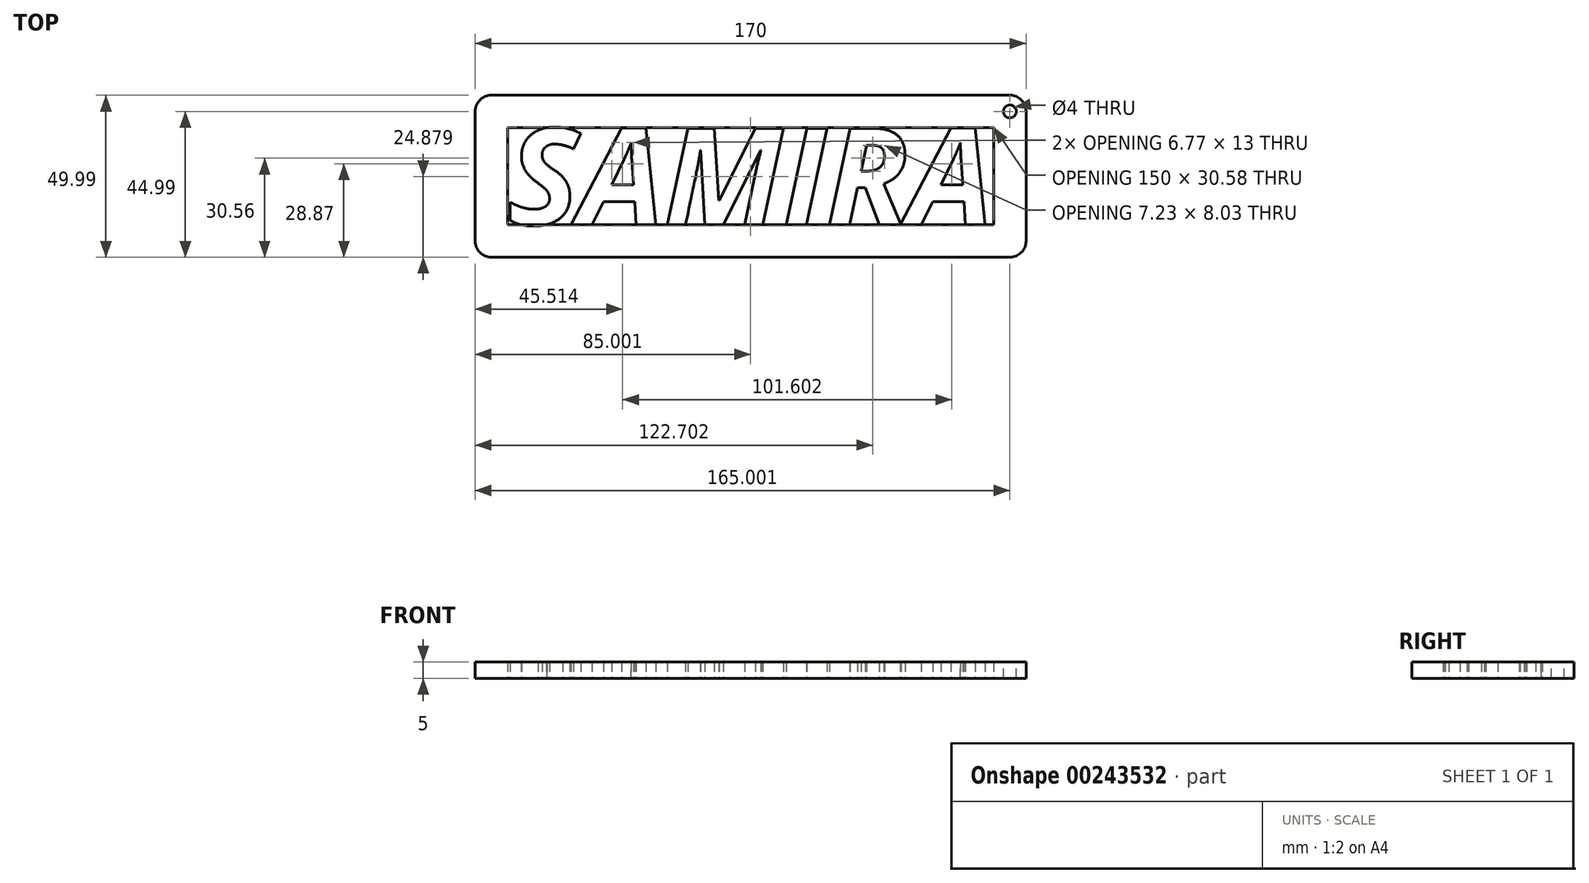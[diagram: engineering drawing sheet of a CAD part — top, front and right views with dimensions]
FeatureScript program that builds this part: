
annotation { "Feature Type Name" : "Feature", "Feature Type Description" : "" }
export const myFeature = defineFeature(function(context is Context, id is Id, definition is map)
    precondition{}
    {
        {
            var Q0;
            Q0=qCreatedBy(makeId("Top.planeOp"),FACE);
            var sketch = newSketch(context, id + "F0", { "sketchPlane" : qUnion([Q0])});
            skText(sketch, "E0", { "text": "SAMIRA", "fontName": "OpenSans-BoldItalic.ttf"});
            skLineSegment(sketch, "E1.bottom", {"start": v(-105.66, 38.68) * mm, "end": v(44.34, 38.68) * mm});
            skLineSegment(sketch, "E1.top", {"start": v(-105.66, 8.69) * mm, "end": v(44.34, 8.69) * mm});
            skLineSegment(sketch, "E1.left", {"start": v(-105.66, 38.68) * mm, "end": v(-105.66, 8.69) * mm});
            skLineSegment(sketch, "E1.right", {"start": v(44.34, 38.68) * mm, "end": v(44.34, 8.69) * mm});
            skLineSegment(sketch, "E2.bottom", {"start": v(-115.66, 48.68) * mm, "end": v(54.34, 48.68) * mm});
            skLineSegment(sketch, "E2.top", {"start": v(-115.66, -1.31) * mm, "end": v(54.34, -1.31) * mm});
            skLineSegment(sketch, "E2.left", {"start": v(-115.66, 48.68) * mm, "end": v(-115.66, -1.31) * mm});
            skLineSegment(sketch, "E2.right", {"start": v(54.34, 48.68) * mm, "end": v(54.34, -1.31) * mm});
            const initialGuessF0  = {"E0": [-0.10566, 0.00869, 1, 0, 0.03]};
            skSetInitialGuess(sketch, initialGuessF0);
            skSolve(sketch);
        }
        {
            var Q0;
            {var subQ9=sQuery(id+"F0.wireOp",EDGE,"E0.sketch_text.stroke-0");Q0=makeQuery(id+"F0.imprint","IMPRINT",FACE,{"disambiguationData":[TD([[makeQuery(id+"F0.imprint","IMPRINT",EDGE,{"derivedFrom":subQ9}),-1.0]])]});}
            var Q1;
            Q1=makeQuery(id+"F0.imprint","IMPRINT",FACE,{"disambiguationData":[TD([[makeQuery(id+"F0.imprint","IMPRINT",EDGE,{"derivedFrom":sQuery(id+"F0.wireOp",EDGE,"E0.sketch_text.stroke-24")}),-1.0]])]});
            var Q2;
            Q2=makeQuery(id+"F0.imprint","IMPRINT",FACE,{"disambiguationData":[TD([[makeQuery(id+"F0.imprint","IMPRINT",EDGE,{"derivedFrom":sQuery(id+"F0.wireOp",EDGE,"E0.sketch_text.stroke-38")}),-1.0]])]});
            var Q3;
            {var subQ0=sQuery(id+"F0.wireOp",EDGE,"E0.sketch_text.stroke-56");Q3=makeQuery(id+"F0.imprint","IMPRINT",FACE,{"disambiguationData":[TD([[makeQuery(id+"F0.imprint","IMPRINT",EDGE,{"derivedFrom":subQ0}),-1.0]])]});}
            var Q4;
            Q4=makeQuery(id+"F0.imprint","IMPRINT",FACE,{"disambiguationData":[TD([[makeQuery(id+"F0.imprint","IMPRINT",EDGE,{"derivedFrom":sQuery(id+"F0.wireOp",EDGE,"E0.sketch_text.stroke-60")}),-1.0]])]});
            var Q5;
            Q5=makeQuery(id+"F0.imprint","IMPRINT",FACE,{"disambiguationData":[TD([[makeQuery(id+"F0.imprint","IMPRINT",EDGE,{"derivedFrom":sQuery(id+"F0.wireOp",EDGE,"E0.sketch_text.stroke-79")}),-1.0]])]});
            extrude(context, id + "F1", {"entities" : qUnion([Q0, Q1, Q2, Q3, Q4, Q5]), "depth" : 5 * mm});
        }
        {
            var Q0;
            Q0 = qSketchRegion(id + "F0", true);
            extrude(context, id + "F2", {"entities" : qUnion([Q0]), "depth" : 5 * mm});
        }
        {
            var Q0;
            Q0=makeQuery(id+"F2.opExtrude","SWEPT_EDGE",EDGE,{"disambiguationData":[OSD([sQuery(id+"F0.wireOp",EDGE,"E2.top"),sQuery(id+"F0.wireOp",EDGE,"E2.left")])]});
            var Q1;
            Q1=makeQuery(id+"F2.opExtrude","SWEPT_EDGE",EDGE,{"disambiguationData":[OSD([sQuery(id+"F0.wireOp",EDGE,"E2.bottom"),sQuery(id+"F0.wireOp",EDGE,"E2.left")])]});
            var Q2;
            Q2=makeQuery(id+"F2.opExtrude","SWEPT_EDGE",EDGE,{"disambiguationData":[OSD([sQuery(id+"F0.wireOp",EDGE,"E2.top"),sQuery(id+"F0.wireOp",EDGE,"E2.right")])]});
            var Q3;
            Q3=makeQuery(id+"F2.opExtrude","SWEPT_EDGE",EDGE,{"disambiguationData":[OSD([sQuery(id+"F0.wireOp",EDGE,"E2.bottom"),sQuery(id+"F0.wireOp",EDGE,"E2.right")])]});
            fillet(context, id + "F3", {"entities" : qUnion([Q0, Q1, Q2, Q3]), "radius" : 5 * mm, "tangentPropagation" : true, "allowEdgeOverflow" : false});
        }
        {
            var Q0;
            Q0=makeQuery(id+"F2.opExtrude","CAP_FACE",FACE,{"disambiguationData":[OSD([sQuery(id+"F0.wireOp",EDGE,"E0.sketch_text.stroke-1"),sQuery(id+"F0.wireOp",EDGE,"E0.sketch_text.stroke-2"),sQuery(id+"F0.wireOp",EDGE,"E0.sketch_text.stroke-14"),sQuery(id+"F0.wireOp",EDGE,"E0.sketch_text.stroke-15"),sQuery(id+"F0.wireOp",EDGE,"E1.bottom"),sQuery(id+"F0.wireOp",EDGE,"E1.top"),sQuery(id+"F0.wireOp",EDGE,"E1.left"),sQuery(id+"F0.wireOp",EDGE,"E1.right"),sQuery(id+"F0.wireOp",EDGE,"E2.bottom"),sQuery(id+"F0.wireOp",EDGE,"E2.top"),sQuery(id+"F0.wireOp",EDGE,"E2.left"),sQuery(id+"F0.wireOp",EDGE,"E2.right")])],"isStart":false});
            var sketch = newSketch(context, id + "F4", { "sketchPlane" : qUnion([Q0])});
            skCircle(sketch, "E3", {"center": v(49.34, 43.68) * mm, "radius": 2 * mm});
            skSolve(sketch);
        }
        {
            var Q0;
            Q0=makeQuery(id+"F4.imprint","IMPRINT",FACE,{"disambiguationData":[TD([[makeQuery(id+"F4.imprint","IMPRINT",EDGE,{"derivedFrom":sQuery(id+"F4.wireOp",EDGE,"E3")}),1.0]])]});
            extrude(context, id + "F5", {"entities" : qUnion([Q0]), "operationType" : NewBodyOperationType.REMOVE, "oppositeDirection" : true, "depth" : 25 * mm});
        }
    });
